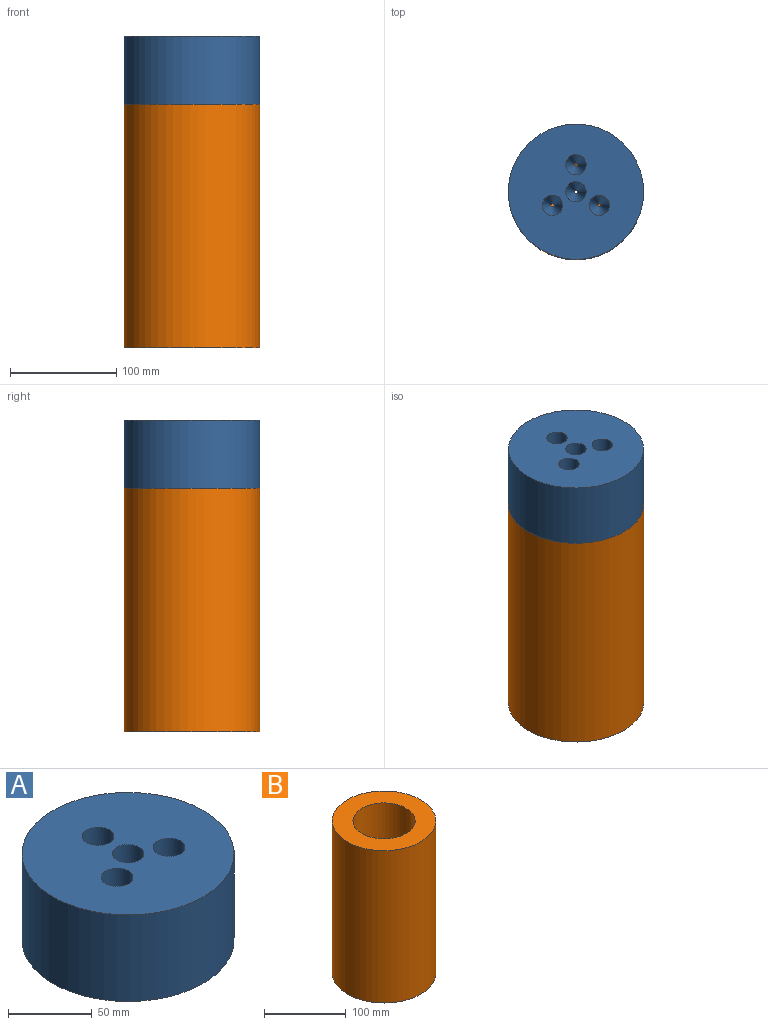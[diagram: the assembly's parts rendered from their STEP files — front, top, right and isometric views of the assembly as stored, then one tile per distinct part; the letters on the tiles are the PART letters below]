
ASSEMBLY  parts=2 mates=1
PART A: 16 faces, bbox 127x127x63.5 mm
  f0: cone r=25.4mm half-angle=45deg, axis (0,0,-1), area 3566mm2, adj f3,f4,f5,f7,f10
  f1: cylinder r=63.5mm len=127mm, axis (0,0,-1), area 25335.4mm2, adj f2,f3
  f2: plane 127x127mm, normal (0,0,1), area 11527.6mm2, adj f1,f6,f8,f9,f11
  f3: plane 127x127mm, normal (0,0,-1), area 8107.3mm2, adj f0,f1
  f4: plane 50.8x50.75mm, normal (0,0,-1), area 2007.2mm2, adj f0,f12,f13,f14,f15
  f5: cylinder r=1.59mm len=2.99mm, axis (0,0,1), area 5.2mm2, adj f0,f12
  f6: cylinder r=9.53mm len=25.4mm, axis (0,0,1), area 1520.1mm2, adj f2,f12
  f7: cylinder r=1.59mm len=2.99mm, axis (0,0,1), area 5.2mm2, adj f0,f15
  f8: cylinder r=9.53mm len=25.4mm, axis (0,0,1), area 1520.1mm2, adj f2,f15
  f9: cylinder r=9.53mm len=25.4mm, axis (0,0,1), area 1520.1mm2, adj f2,f14
  f10: cylinder r=1.59mm len=3.18mm, axis (0,0,1), area 5.2mm2, adj f0,f13
  f11: cylinder r=9.53mm len=25.4mm, axis (0,0,1), area 1520.1mm2, adj f2,f13
  f12: cone r=1.59mm half-angle=17.4deg, axis (0,0,1), area 929mm2, adj f4,f5,f6
  f13: cone r=1.59mm half-angle=17.4deg, axis (0,0,1), area 929mm2, adj f4,f10,f11
  f14: cone r=1.59mm half-angle=17.4deg, axis (0,0,1), area 929mm2, adj f4,f9
  f15: cone r=1.59mm half-angle=17.4deg, axis (0,0,1), area 929mm2, adj f4,f7,f8
PART B: 5 faces, bbox 127x127x228.6 mm
  f0: cylinder r=63.5mm len=228.6mm, axis (0,0,-1), area 91207.3mm2, adj f1,f2
  f1: plane 127x127mm, normal (0,0,1), area 8107.3mm2, adj f0,f3
  f2: cone r=12.7mm half-angle=21.8deg, axis (0,0,-1), area 32744.4mm2, adj f0,f4
  f3: cylinder r=38.1mm len=88.9mm, axis (0,0,1), area 21281.7mm2, adj f1,f4
  f4: cone r=12.7mm half-angle=63.4deg, axis (0,0,1), area 4532.1mm2, adj f2,f3
PLACE A t=(-94.88,3.26,226.13)mm
PLACE B t=(-94.88,3.26,-2.47)mm
MATE fastened B.f0 <-> A.f1  axis (0,0,1) through (-94.88,3.26,226.13)mm
